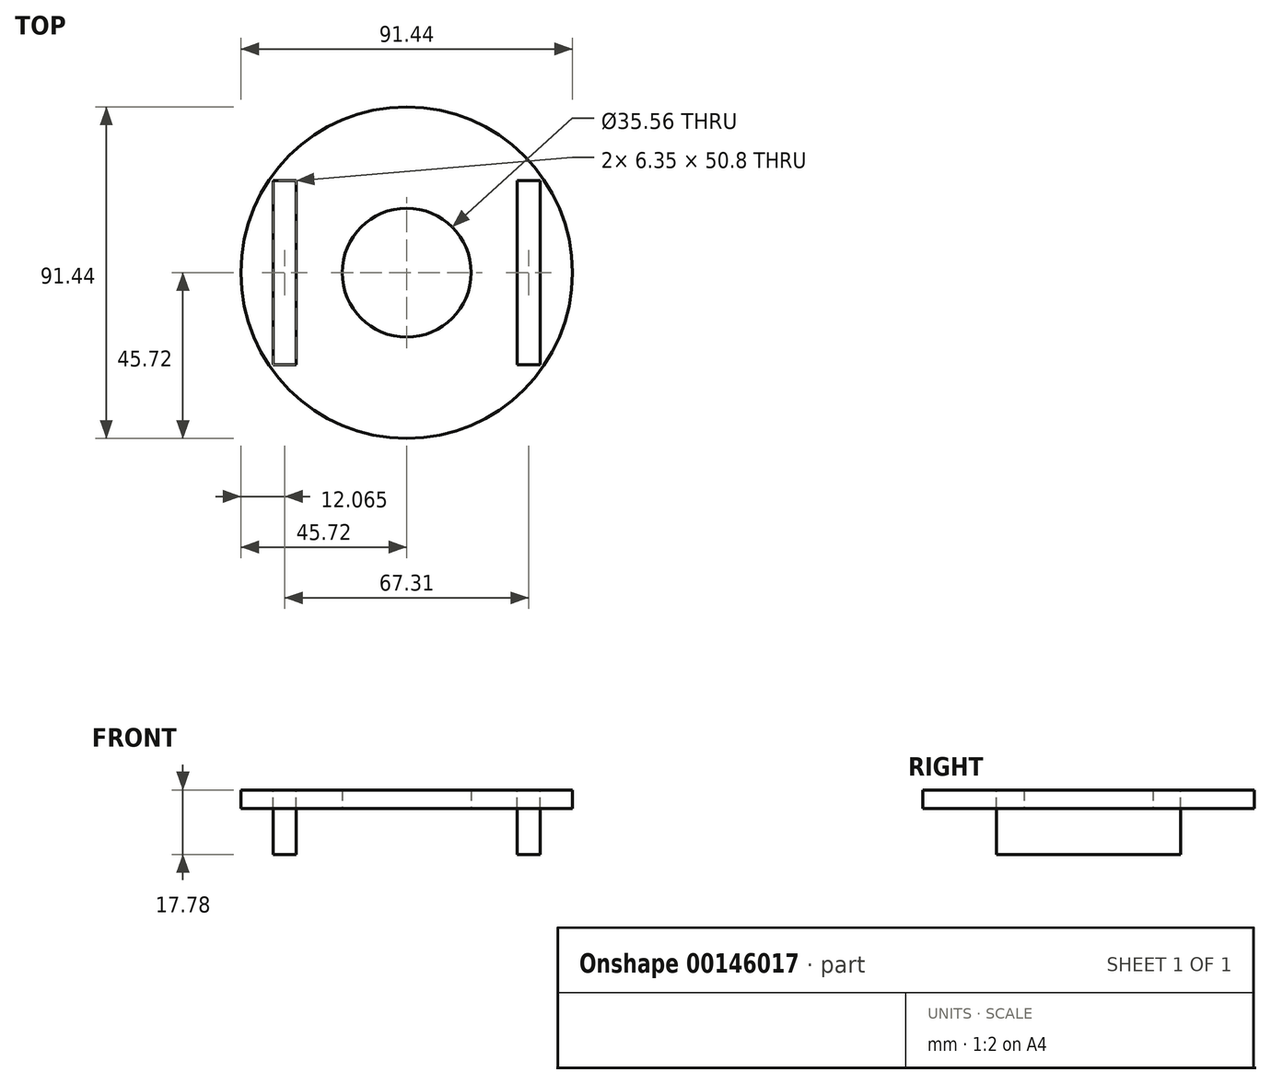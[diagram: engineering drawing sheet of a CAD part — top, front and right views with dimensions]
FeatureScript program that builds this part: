
annotation { "Feature Type Name" : "Feature", "Feature Type Description" : "" }
export const myFeature = defineFeature(function(context is Context, id is Id, definition is map)
    precondition{}
    {
        {
            var Q0;
            Q0=qCreatedBy(makeId("Top.planeOp"),FACE);
            var sketch = newSketch(context, id + "F0", { "sketchPlane" : qUnion([Q0])});
            skCircle(sketch, "E0", {"center": v(0, 0) * mm, "radius": 45.72 * mm});
            skCircle(sketch, "E1", {"center": v(0, 0) * mm, "radius": 17.78 * mm});
            skLineSegment(sketch, "E2", {"start": v(0, 45.72) * mm, "end": v(0, -45.72) * mm, "construction": true});
            skLineSegment(sketch, "E3", {"start": v(45.72, 0) * mm, "end": v(-45.72, 0) * mm, "construction": true});
            skLineSegment(sketch, "E4.bottom", {"start": v(30.48, 0) * mm, "end": v(36.83, 0) * mm});
            skLineSegment(sketch, "E4.top", {"start": v(30.48, 25.4) * mm, "end": v(36.83, 25.4) * mm});
            skLineSegment(sketch, "E4.left", {"start": v(30.48, 0) * mm, "end": v(30.48, 25.4) * mm});
            skLineSegment(sketch, "E4.right", {"start": v(36.83, 0) * mm, "end": v(36.83, 25.4) * mm});
            skLineSegment(sketch, "E5.MirrorCS", {"start": v(30.48, -25.4) * mm, "end": v(36.83, -25.4) * mm});
            skLineSegment(sketch, "E6.MirrorCS", {"start": v(36.83, 0) * mm, "end": v(36.83, -25.4) * mm});
            skLineSegment(sketch, "E7.MirrorCS", {"start": v(30.48, 0) * mm, "end": v(30.48, -25.4) * mm});
            skLineSegment(sketch, "E8.MirrorCS", {"start": v(-36.83, 0) * mm, "end": v(-36.83, 25.4) * mm});
            skLineSegment(sketch, "E9.MirrorCS", {"start": v(-30.48, 0) * mm, "end": v(-30.48, 25.4) * mm});
            skLineSegment(sketch, "E10.MirrorCS", {"start": v(-30.48, 25.4) * mm, "end": v(-36.83, 25.4) * mm});
            skLineSegment(sketch, "E11.MirrorCS", {"start": v(-36.83, 0) * mm, "end": v(-36.83, -25.4) * mm});
            skLineSegment(sketch, "E12.MirrorCS", {"start": v(-30.48, 0) * mm, "end": v(-30.48, -25.4) * mm});
            skLineSegment(sketch, "E13.MirrorCS", {"start": v(-30.48, -25.4) * mm, "end": v(-36.83, -25.4) * mm});
            skSolve(sketch);
        }
        {
            var Q0;
            Q0 = qSketchRegion(id + "F0", true);
            extrude(context, id + "F1", {"entities" : qUnion([Q0]), "depth" : 5.08 * mm});
        }
        {
            var Q0;
            Q0=makeQuery(id+"F1.opExtrude","CAP_FACE",FACE,{"disambiguationData":[OSD([sQuery(id+"F0.wireOp",EDGE,"E0"),sQuery(id+"F0.wireOp",EDGE,"E1")])],"isStart":true});
            var sketch = newSketch(context, id + "F2", { "sketchPlane" : qUnion([Q0])});
            skSolve(sketch);
        }
        {
            var Q0;
            Q0=makeQuery(id+"F2.imprint","IMPRINT",FACE,{"disambiguationData":[TD([[makeQuery(id+"F2.imprint","IMPRINT",EDGE,{"derivedFrom":makeQuery(id+"F1.opExtrude","CAP_EDGE",EDGE,{"disambiguationData":[OSD([sQuery(id+"F0.wireOp",EDGE,"E4.top")])],"isStart":true})}),1.0]])]});
            var Q1;
            Q1=makeQuery(id+"F2.imprint","IMPRINT",FACE,{"disambiguationData":[TD([[makeQuery(id+"F2.imprint","IMPRINT",EDGE,{"derivedFrom":makeQuery(id+"F1.opExtrude","CAP_EDGE",EDGE,{"disambiguationData":[OSD([sQuery(id+"F0.wireOp",EDGE,"E10.MirrorCS")])],"isStart":true})}),-1.0]])]});
            extrude(context, id + "F3", {"entities" : qUnion([Q0, Q1]), "depth" : 12.7 * mm, "hasSecondDirection" : true, "secondDirectionOppositeDirection" : true, "secondDirectionDepth" : 5.08 * mm});
        }
    });
